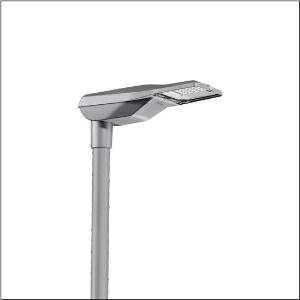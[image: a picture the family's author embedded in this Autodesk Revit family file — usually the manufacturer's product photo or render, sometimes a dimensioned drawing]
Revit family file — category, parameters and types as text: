
# Revit family: streetlight_sl_21_iq_micro___st1_5a_5xe1p31g08cb_4914
name_source: partatom
category: Lighting Fixtures
units: mm (PartAtom-declared; Revit-internal decimal feet)

## family parameters
Cut with Voids When Loaded = No
Host = Face
Light Source = No
Part Type = Normal
Room Calculation Point = No
Round Connector Dimension = Use Diameter
Shared = No

## types (1)
- --- (1 x LED, 2820 lm, 19.4 W, 3000K)
    Apparent Load = 19 VA
    CIE Flux Codes = 22 53 95 100 100
    Color Rendering = 70
    Color Temperature = 3000K
    Default Elevation = 1800 mm
    Description = Streetlight SL 21 iQ micro, mast luminaire, primary light control with lens, of PMMA, primary optical cover: cover, of toughened safety glass, transparent, light distribution: ST1.5a, light emission: direct distribution, primary light characteristic: asymmetric, installation type: post-top, side-entry, LED, High Power LED, rated luminous flux: 2.820lm, luminous efficacy: 145lm/W, light colour: 730, colour temperature: 3000K, control: Street-Remote, Auto-Match, Temp-Guard, Lumen-Switch, Night-Set, Smart-Wire, Light-Fading, Desk-Remote (wireless, voltage-free reading and setting of iQ features in the workshop via application-optimized NFC function/RFID function), optimised constant luminous flux control (CLO 2.0), presetting dimming linear, mains connection: 220..240V, AC, 50/60Hz, start of lifetime: 19W, end of service life: 20W, reduction: 10W, luminaire housing, of diecast aluminium, powder-coated, Siteco® metallic grey (DB 702S), corrosivity category C5 mid according to DIN EN ISO 12944, please order mast flange separately, inclination adjustable: 0°, 5°, 10°, 15°, sealing non-destructively replaceable, multi-level sealing system, length: 528mm, width: 235mm, height: 110mm, mast flange for spigot size: 42mm (side-entry): 5XC10008XM4, 60/48mm (side-entry/post-top): 5XC10108XM2, 76/60mm (side-entry/post-top): 5XC10108XM1, protection rating (complete): IP66, insulation class (complete): insulation class II (safety insulation), certification: CE, ENEC, ENEC+, VDE, impact resistance: IK09, permissible operating ambient temperature for outdoor applications: -40..+50°C, standard-compliant lighting for roads and squares, packaging unit: 1 piece

Light Distribution: ST1.5a
    Height = 110 mm
    Lamp = 1 x LED
    Lamp Light Flux = 2820 lm
    Lamp Power = 19.4 W
    Lamp count = 1
    Length = 528 mm
    Luminous efficacy = 145 lm/W
    Manufacturer = Siteco
    ModVariant = No
    Model = 5XE1P31G08CB
    Number of Poles = 1
    OnlyDefault = Yes
    Power Factor = 1
    Product Name = Streetlight SL 21 iQ micro | ST1.5a
    Product group = mast luminaire | pylon top
    ProductGroupID = 6100
    Protection Class = Protection class II
    Protection Degree = IP 66
    RLX_Detail_Level = 1
    RLX_Emergency_Light_Flux = 0 lm
    RLX_Emergency_Type = 0
    RLX_Emergency_Type_DB = No
    RlxData = <blob elided: 102105 chars, md5=a8be1635>
    Socket = socket
    Standby Power = 0 W
    System Light Flux = 2820 lm
    System Power = 19 W
    Type Comments = factory setting: luminous flux: 100 % | dim-lin: 254 | 387 mA
    Type Image = l_1006881.jpg
    URL = http://relux.com
    VarID = @adj_069397
    Voltage = 0 V
    Weight = 0.00 kg
    Width = 235 mm

## geometry (parser evidence)
native form markers: Blend x4, Sweep x10
no freeform markers — native parametric forms only
